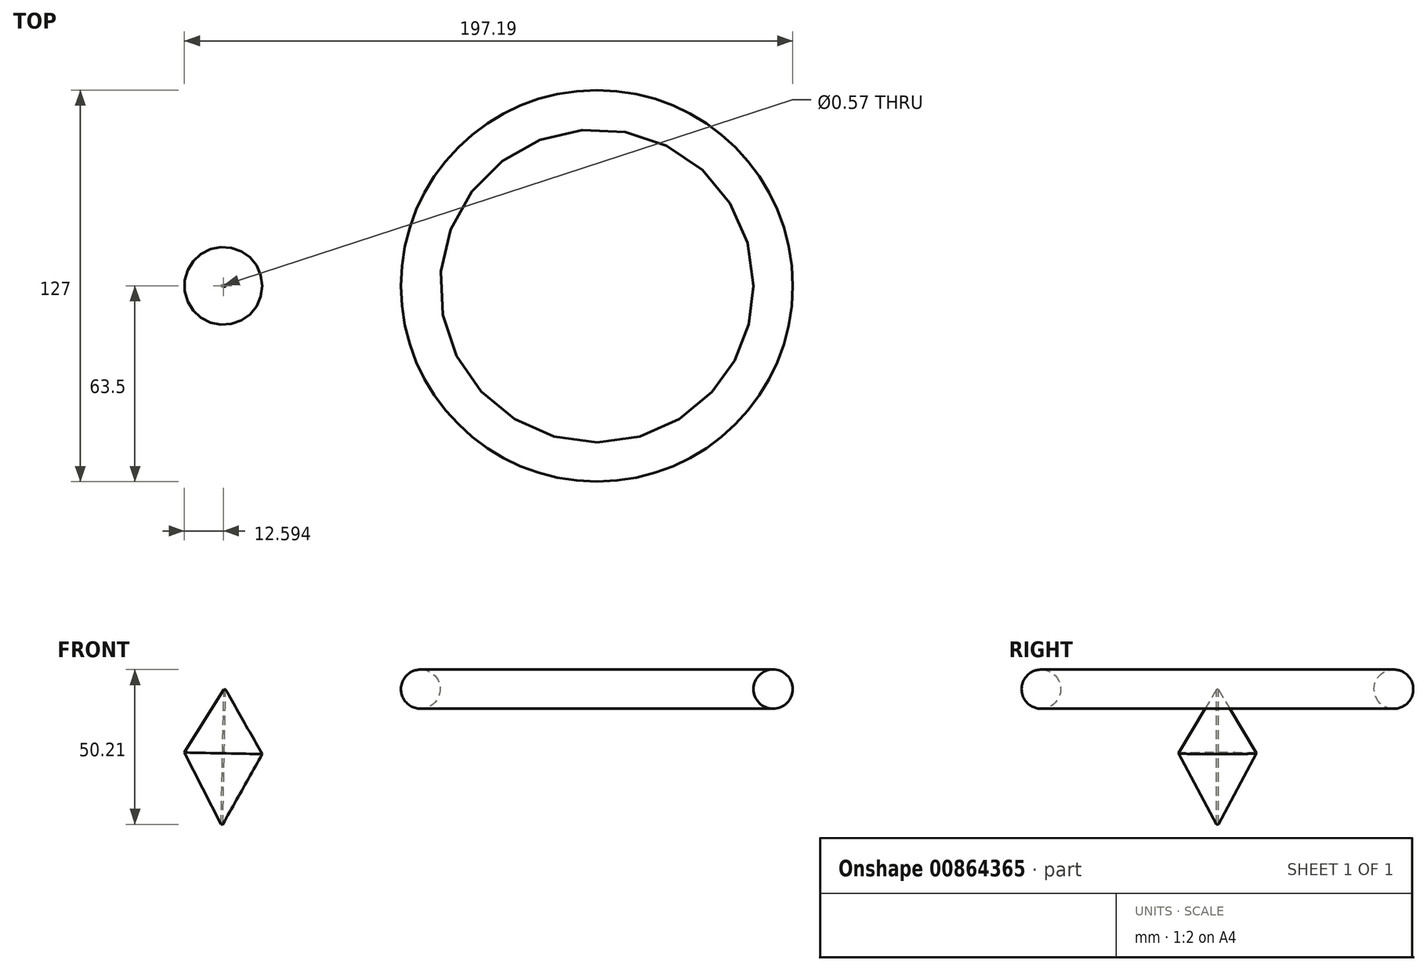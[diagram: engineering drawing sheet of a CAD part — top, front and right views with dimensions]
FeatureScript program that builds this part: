
annotation { "Feature Type Name" : "Feature", "Feature Type Description" : "" }
export const myFeature = defineFeature(function(context is Context, id is Id, definition is map)
    precondition{}
    {
        {
            var Q0;
            Q0=qCreatedBy(makeId("Front.planeOp"),FACE);
            var sketch = newSketch(context, id + "F0", { "sketchPlane" : qUnion([Q0])});
            skCircle(sketch, "E0", {"center": v(9.54, 2.13) * mm, "radius": 6.35 * mm});
            skLineSegment(sketch, "E1", {"start": v(66.69, 121) * mm, "end": v(66.69, -169.25) * mm});
            skSolve(sketch);
        }
        {
            var Q0;
            Q0=makeQuery(id+"F0.imprint","IMPRINT",FACE,{"disambiguationData":[TD([[makeQuery(id+"F0.imprint","IMPRINT",EDGE,{"derivedFrom":sQuery(id+"F0.wireOp",EDGE,"E0")}),1.0]])]});
            var Q1;
            Q1=sQuery(id+"F0.wireOp",EDGE,"E1");
            revolve(context, id + "F1", {"surfaceOperationType" : NewSurfaceOperationType.NEW, "entities" : qUnion([Q0]), "axis" : qUnion([Q1]), "revolveType" : RevolveType.FULL});
        }
        {
            var Q0;
            Q0=qCreatedBy(makeId("Front.planeOp"),FACE);
            var sketch = newSketch(context, id + "F2", { "sketchPlane" : qUnion([Q0])});
            skLineSegment(sketch, "E2", {"start": v(-52.35, 65.74) * mm, "end": v(-40.45, 44.78) * mm});
            skLineSegment(sketch, "E3", {"start": v(-40.45, 44.78) * mm, "end": v(-53.25, 22.01) * mm});
            skLineSegment(sketch, "E4", {"start": v(-53.25, 22.01) * mm, "end": v(-52.35, 65.74) * mm});
            skLineSegment(sketch, "E5", {"start": v(-52.35, 79.58) * mm, "end": v(-53.8, 9.33) * mm, "construction": true});
            skSolve(sketch);
        }
        {
            var Q0;
            Q0=makeQuery(id+"F2.imprint","IMPRINT",FACE,{"disambiguationData":[TD([[makeQuery(id+"F2.imprint","IMPRINT",EDGE,{"derivedFrom":sQuery(id+"F2.wireOp",EDGE,"E2")}),-1.0]])]});
            var Q1;
            Q1=sQuery(id+"F2.wireOp",EDGE,"E5");
            revolve(context, id + "F3", {"surfaceOperationType" : NewSurfaceOperationType.NEW, "entities" : qUnion([Q0]), "axis" : qUnion([Q1]), "revolveType" : RevolveType.FULL});
        }
        {
            var Q0;
            Q0=makeQuery(id+"F3.opRevolve","SWEPT_BODY",BODY,{"disambiguationData":[OSD([sQuery(id+"F2.wireOp",EDGE,"E2"),sQuery(id+"F2.wireOp",EDGE,"E3"),sQuery(id+"F2.wireOp",EDGE,"E4")])]});
            var Q1;
            Q1=makeQuery(id+"F3.opRevolve","SWEPT_EDGE",EDGE,{"disambiguationData":[OSD([sQuery(id+"F2.wireOp",EDGE,"E2"),sQuery(id+"F2.wireOp",EDGE,"E4")])]});
            var Q2;
            Q2=makeQuery(id+"F3.opRevolve","SWEPT_FACE",FACE,{"disambiguationData":[OSD([sQuery(id+"F2.wireOp",EDGE,"E3")])]});
            transform(context, id + "F4", {"entities" : qUnion([Q0]), "transformType" : TransformType.TRANSLATION_DISTANCE, "transformDirection" : qUnion([Q2]), "distance" : 63.75 * mm, "oppositeDirection" : true, "makeCopy" : false});
        }
    });
